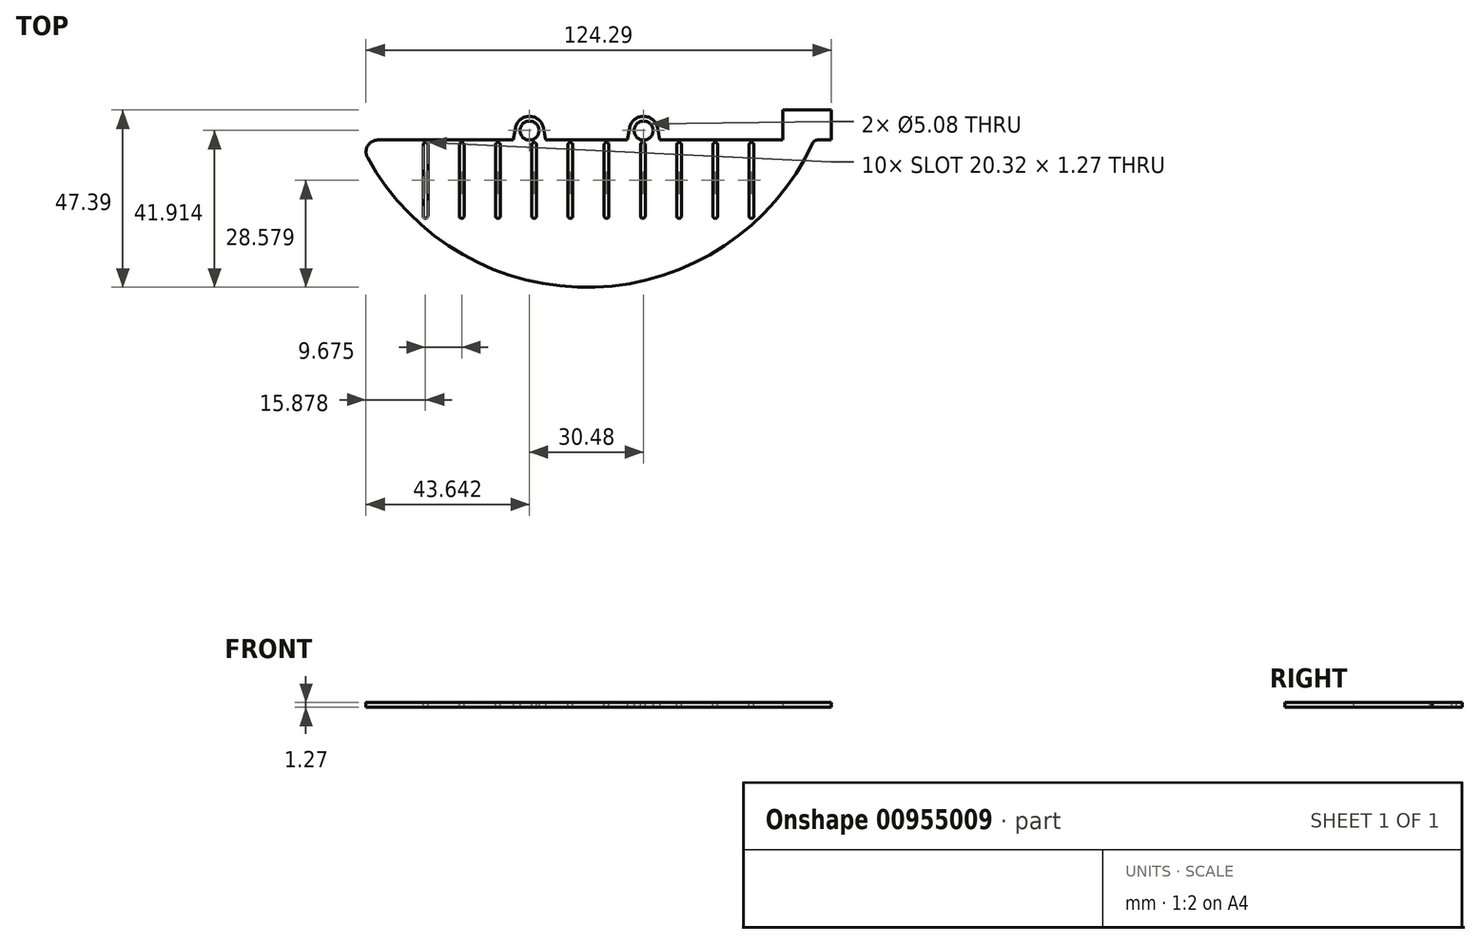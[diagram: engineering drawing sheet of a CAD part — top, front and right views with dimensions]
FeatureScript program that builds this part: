
annotation { "Feature Type Name" : "Feature", "Feature Type Description" : "" }
export const myFeature = defineFeature(function(context is Context, id is Id, definition is map)
    precondition{}
    {
        {
            var Q0;
            Q0=qCreatedBy(makeId("Top.planeOp"),FACE);
            var sketch = newSketch(context, id + "F0", { "sketchPlane" : qUnion([Q0])});
            skArc(sketch, "E0.0", {"start": v(-97.26, -15.73) * mm, "mid": v(-36.55, -50.37) * mm, "end": v(21.73, -11.77) * mm});
            skArc(sketch, "E0.1", {"start": v(-94.47, -11.04) * mm, "mid": v(-97.2, -12.6) * mm, "end": v(-97.26, -15.73) * mm});
            skLineSegment(sketch, "E0.2", {"start": v(-94.47, -11.04) * mm, "end": v(-64.17, -11.04) * mm});
            skLineSegment(sketch, "E0.3", {"start": v(-64.17, -11.04) * mm, "end": v(-58.32, -11.04) * mm});
            skLineSegment(sketch, "E0.4", {"start": v(-57.76, -7.83) * mm, "end": v(-58.32, -11.04) * mm});
            skArc(sketch, "E0.5", {"start": v(-50.26, -7.83) * mm, "mid": v(-54, -4.69) * mm, "end": v(-57.76, -7.83) * mm});
            skLineSegment(sketch, "E0.6", {"start": v(-50.26, -7.83) * mm, "end": v(-49.7, -11.04) * mm});
            skLineSegment(sketch, "E0.7", {"start": v(-49.7, -11.04) * mm, "end": v(-33.69, -11.04) * mm});
            skLineSegment(sketch, "E0.8", {"start": v(-33.69, -11.04) * mm, "end": v(-27.84, -11.04) * mm});
            skLineSegment(sketch, "E0.9", {"start": v(-27.28, -7.83) * mm, "end": v(-27.84, -11.04) * mm});
            skArc(sketch, "E0.10", {"start": v(-27.28, -7.83) * mm, "mid": v(-23.53, -4.69) * mm, "end": v(-19.78, -7.83) * mm});
            skLineSegment(sketch, "E0.11", {"start": v(-19.78, -7.83) * mm, "end": v(-19.21, -11.04) * mm});
            skLineSegment(sketch, "E0.12", {"start": v(-19.21, -11.04) * mm, "end": v(13.69, -11.04) * mm});
            skCircle(sketch, "E0.13", {"center": v(-23.53, -8.5) * mm, "radius": 2.54 * mm});
            skCircle(sketch, "E0.14", {"center": v(-54, -8.5) * mm, "radius": 2.54 * mm});
            skLineSegment(sketch, "E0.15", {"start": v(13.69, -3.02) * mm, "end": v(13.69, -11.04) * mm});
            skLineSegment(sketch, "E0.16", {"start": v(15.2, -3.02) * mm, "end": v(26.64, -3.02) * mm});
            skLineSegment(sketch, "E0.17", {"start": v(15.2, -3.02) * mm, "end": v(13.69, -3.02) * mm});
            skArc(sketch, "E0.20", {"start": v(22.88, -11.04) * mm, "mid": v(22.2, -11.24) * mm, "end": v(21.73, -11.77) * mm});
            skLineSegment(sketch, "E0.21", {"start": v(25.53, -11.04) * mm, "end": v(22.88, -11.04) * mm});
            skFitSpline(sketch, "E0.22", {"points": [v(26.64, -11.04) * mm, v(26.27, -11.04) * mm, v(25.9, -11.04) * mm, v(25.53, -11.04) * mm]});
            skLineSegment(sketch, "E1", {"start": v(26.64, -11.04) * mm, "end": v(26.64, -3.02) * mm});
            skSolve(sketch);
        }
        {
            var Q0;
            Q0 = qSketchRegion(id + "F0", true);
            extrude(context, id + "F1", {"entities" : qUnion([Q0]), "depth" : 1.27 * mm, "offsetDistance" : 25.4 * mm});
        }
        {
            var Q0;
            Q0=makeQuery(id+"F1.opExtrude","CAP_FACE",FACE,{"disambiguationData":[OSD([sQuery(id+"F0.wireOp",EDGE,"E0.0"),sQuery(id+"F0.wireOp",EDGE,"E0.1"),sQuery(id+"F0.wireOp",EDGE,"E0.2"),sQuery(id+"F0.wireOp",EDGE,"E0.3"),sQuery(id+"F0.wireOp",EDGE,"E0.4"),sQuery(id+"F0.wireOp",EDGE,"E0.5"),sQuery(id+"F0.wireOp",EDGE,"E0.6"),sQuery(id+"F0.wireOp",EDGE,"E0.7"),sQuery(id+"F0.wireOp",EDGE,"E0.8"),sQuery(id+"F0.wireOp",EDGE,"E0.9"),sQuery(id+"F0.wireOp",EDGE,"E0.10"),sQuery(id+"F0.wireOp",EDGE,"E0.11"),sQuery(id+"F0.wireOp",EDGE,"E0.12"),sQuery(id+"F0.wireOp",EDGE,"E0.13"),sQuery(id+"F0.wireOp",EDGE,"E0.14"),sQuery(id+"F0.wireOp",EDGE,"E0.15"),sQuery(id+"F0.wireOp",EDGE,"E0.16"),sQuery(id+"F0.wireOp",EDGE,"E0.17"),sQuery(id+"F0.wireOp",EDGE,"E0.20"),sQuery(id+"F0.wireOp",EDGE,"E0.21"),sQuery(id+"F0.wireOp",EDGE,"E0.22"),sQuery(id+"F0.wireOp",EDGE,"E1")])],"isStart":false});
            var sketch = newSketch(context, id + "F2", { "sketchPlane" : qUnion([Q0])});
            skLineSegment(sketch, "E2.left", {"start": v(-82.4, -12.3) * mm, "end": v(-82.4, -31.36) * mm});
            skLineSegment(sketch, "E2.right", {"start": v(-81.14, -12.3) * mm, "end": v(-81.14, -31.36) * mm});
            skPoint(sketch, "E2.middle", {"position": v(-81.77, -21.83) * mm});
            skArc(sketch, "E3", {"start": v(-81.14, -12.3) * mm, "mid": v(-81.77, -11.67) * mm, "end": v(-82.4, -12.3) * mm});
            skArc(sketch, "E4", {"start": v(-82.4, -31.36) * mm, "mid": v(-81.77, -32) * mm, "end": v(-81.14, -31.36) * mm});
            skLineSegment(sketch, "E5.1.0.0", {"start": v(-72.73, -12.3) * mm, "end": v(-72.73, -31.36) * mm});
            skLineSegment(sketch, "E5.1.0.1", {"start": v(-71.46, -12.3) * mm, "end": v(-71.46, -31.36) * mm});
            skPoint(sketch, "E5.1.0.2", {"position": v(-72.1, -21.83) * mm});
            skArc(sketch, "E5.1.0.3", {"start": v(-71.46, -12.3) * mm, "mid": v(-72.1, -11.67) * mm, "end": v(-72.73, -12.3) * mm});
            skArc(sketch, "E5.1.0.4", {"start": v(-72.73, -31.36) * mm, "mid": v(-72.1, -32) * mm, "end": v(-71.46, -31.36) * mm});
            skLineSegment(sketch, "E5.2.0.0", {"start": v(-63.06, -12.3) * mm, "end": v(-63.06, -31.36) * mm});
            skLineSegment(sketch, "E5.2.0.1", {"start": v(-61.79, -12.3) * mm, "end": v(-61.79, -31.36) * mm});
            skPoint(sketch, "E5.2.0.2", {"position": v(-62.42, -21.83) * mm});
            skArc(sketch, "E5.2.0.3", {"start": v(-61.79, -12.3) * mm, "mid": v(-62.42, -11.67) * mm, "end": v(-63.06, -12.3) * mm});
            skArc(sketch, "E5.2.0.4", {"start": v(-63.06, -31.36) * mm, "mid": v(-62.42, -32) * mm, "end": v(-61.79, -31.36) * mm});
            skLineSegment(sketch, "E5.3.0.0", {"start": v(-53.38, -12.3) * mm, "end": v(-53.38, -31.36) * mm});
            skLineSegment(sketch, "E5.3.0.1", {"start": v(-52.11, -12.3) * mm, "end": v(-52.11, -31.36) * mm});
            skPoint(sketch, "E5.3.0.2", {"position": v(-52.75, -21.83) * mm});
            skArc(sketch, "E5.3.0.3", {"start": v(-52.11, -12.3) * mm, "mid": v(-52.75, -11.67) * mm, "end": v(-53.38, -12.3) * mm});
            skArc(sketch, "E5.3.0.4", {"start": v(-53.38, -31.36) * mm, "mid": v(-52.75, -32) * mm, "end": v(-52.11, -31.36) * mm});
            skLineSegment(sketch, "E5.4.0.0", {"start": v(-43.7, -12.3) * mm, "end": v(-43.7, -31.36) * mm});
            skLineSegment(sketch, "E5.4.0.1", {"start": v(-42.44, -12.3) * mm, "end": v(-42.44, -31.36) * mm});
            skPoint(sketch, "E5.4.0.2", {"position": v(-43.07, -21.83) * mm});
            skArc(sketch, "E5.4.0.3", {"start": v(-42.44, -12.3) * mm, "mid": v(-43.07, -11.67) * mm, "end": v(-43.7, -12.3) * mm});
            skArc(sketch, "E5.4.0.4", {"start": v(-43.7, -31.36) * mm, "mid": v(-43.07, -32) * mm, "end": v(-42.44, -31.36) * mm});
            skLineSegment(sketch, "E5.5.0.0", {"start": v(-34.03, -12.3) * mm, "end": v(-34.03, -31.36) * mm});
            skLineSegment(sketch, "E5.5.0.1", {"start": v(-32.76, -12.3) * mm, "end": v(-32.76, -31.36) * mm});
            skPoint(sketch, "E5.5.0.2", {"position": v(-33.4, -21.83) * mm});
            skArc(sketch, "E5.5.0.3", {"start": v(-32.76, -12.3) * mm, "mid": v(-33.4, -11.67) * mm, "end": v(-34.03, -12.3) * mm});
            skArc(sketch, "E5.5.0.4", {"start": v(-34.03, -31.36) * mm, "mid": v(-33.4, -32) * mm, "end": v(-32.76, -31.36) * mm});
            skLineSegment(sketch, "E5.6.0.0", {"start": v(-24.36, -12.3) * mm, "end": v(-24.36, -31.36) * mm});
            skLineSegment(sketch, "E5.6.0.1", {"start": v(-23.09, -12.3) * mm, "end": v(-23.09, -31.36) * mm});
            skPoint(sketch, "E5.6.0.2", {"position": v(-23.72, -21.83) * mm});
            skArc(sketch, "E5.6.0.3", {"start": v(-23.09, -12.3) * mm, "mid": v(-23.72, -11.67) * mm, "end": v(-24.36, -12.3) * mm});
            skArc(sketch, "E5.6.0.4", {"start": v(-24.36, -31.36) * mm, "mid": v(-23.72, -32) * mm, "end": v(-23.09, -31.36) * mm});
            skLineSegment(sketch, "E5.7.0.0", {"start": v(-14.68, -12.3) * mm, "end": v(-14.68, -31.36) * mm});
            skLineSegment(sketch, "E5.7.0.1", {"start": v(-13.41, -12.3) * mm, "end": v(-13.41, -31.36) * mm});
            skPoint(sketch, "E5.7.0.2", {"position": v(-14.05, -21.83) * mm});
            skArc(sketch, "E5.7.0.3", {"start": v(-13.41, -12.3) * mm, "mid": v(-14.05, -11.67) * mm, "end": v(-14.68, -12.3) * mm});
            skArc(sketch, "E5.7.0.4", {"start": v(-14.68, -31.36) * mm, "mid": v(-14.05, -32) * mm, "end": v(-13.41, -31.36) * mm});
            skLineSegment(sketch, "E5.8.0.0", {"start": v(-5, -12.3) * mm, "end": v(-5, -31.36) * mm});
            skLineSegment(sketch, "E5.8.0.1", {"start": v(-3.74, -12.3) * mm, "end": v(-3.74, -31.36) * mm});
            skPoint(sketch, "E5.8.0.2", {"position": v(-4.37, -21.83) * mm});
            skArc(sketch, "E5.8.0.3", {"start": v(-3.74, -12.3) * mm, "mid": v(-4.37, -11.67) * mm, "end": v(-5, -12.3) * mm});
            skArc(sketch, "E5.8.0.4", {"start": v(-5, -31.36) * mm, "mid": v(-4.37, -32) * mm, "end": v(-3.74, -31.36) * mm});
            skLineSegment(sketch, "E5.9.0.0", {"start": v(4.67, -12.3) * mm, "end": v(4.67, -31.36) * mm});
            skLineSegment(sketch, "E5.9.0.1", {"start": v(5.94, -12.3) * mm, "end": v(5.94, -31.36) * mm});
            skPoint(sketch, "E5.9.0.2", {"position": v(5.3, -21.83) * mm});
            skArc(sketch, "E5.9.0.3", {"start": v(5.94, -12.3) * mm, "mid": v(5.3, -11.67) * mm, "end": v(4.67, -12.3) * mm});
            skArc(sketch, "E5.9.0.4", {"start": v(4.67, -31.36) * mm, "mid": v(5.3, -32) * mm, "end": v(5.94, -31.36) * mm});
            skLineSegment(sketch, "E5.direction1", {"start": v(-82.4, -31.36) * mm, "end": v(-72.73, -31.36) * mm, "construction": true});
            skSolve(sketch);
        }
        {
            var Q0;
            Q0 = qSketchRegion(id + "F2", true);
            extrude(context, id + "F3", {"entities" : qUnion([Q0]), "operationType" : NewBodyOperationType.REMOVE, "oppositeDirection" : true, "depth" : 25.4 * mm, "offsetDistance" : 25.4 * mm});
        }
    });
